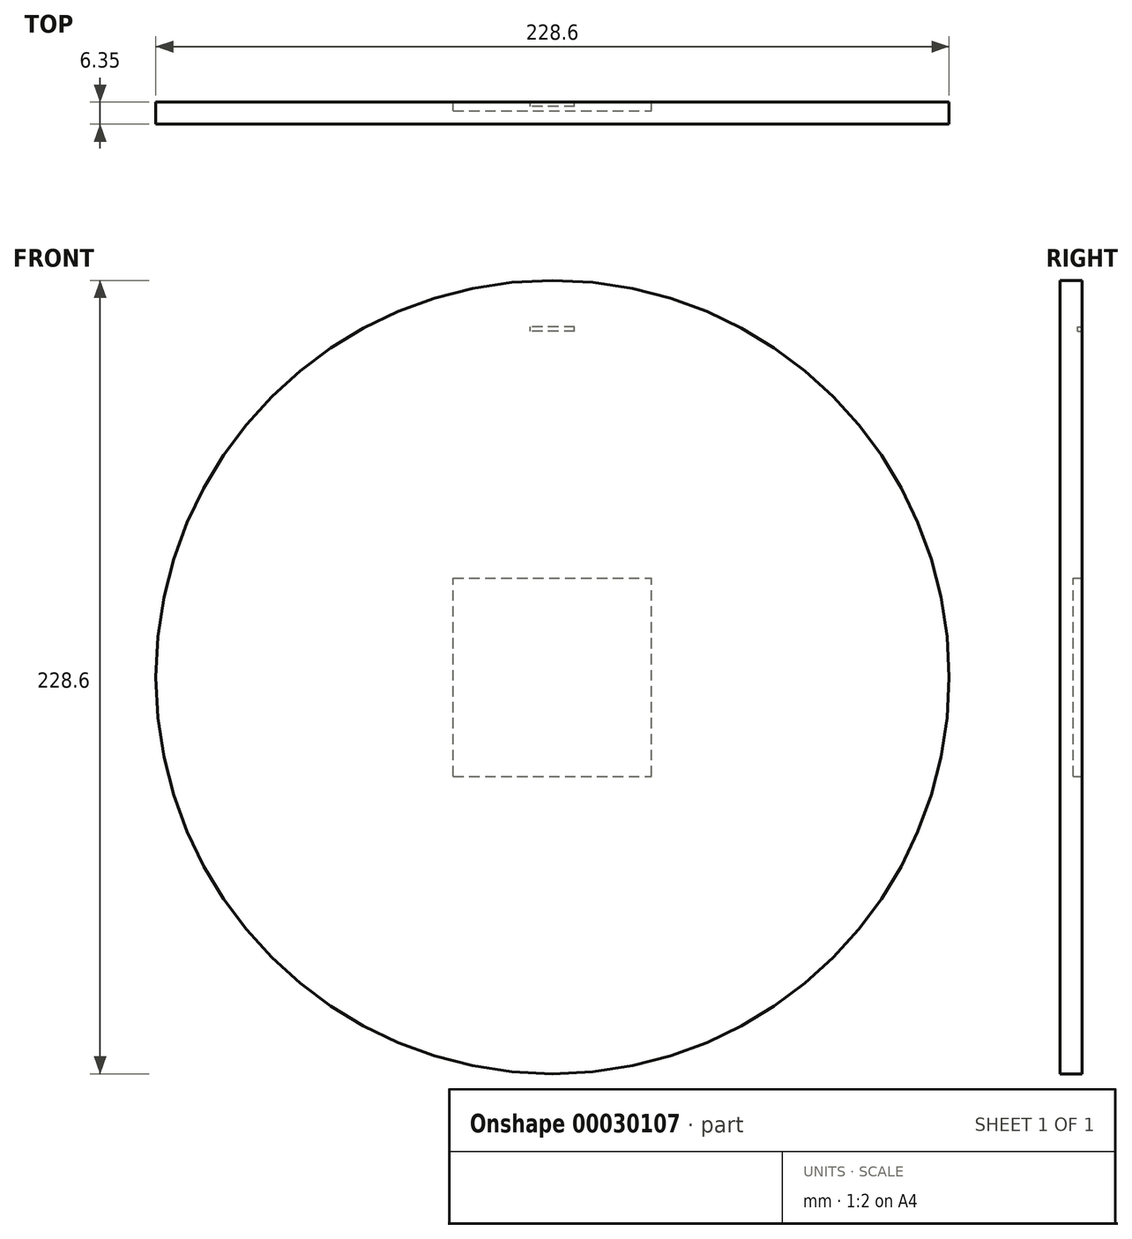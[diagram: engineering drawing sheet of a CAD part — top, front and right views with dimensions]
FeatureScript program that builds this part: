
annotation { "Feature Type Name" : "Feature", "Feature Type Description" : "" }
export const myFeature = defineFeature(function(context is Context, id is Id, definition is map)
    precondition{}
    {
        {
            var Q0;
            Q0=qCreatedBy(makeId("Front.planeOp"),FACE);
            var sketch = newSketch(context, id + "F0", { "sketchPlane" : qUnion([Q0])});
            skCircle(sketch, "E0", {"center": v(0, 0) * mm, "radius": 114.3 * mm});
            skSolve(sketch);
        }
        {
            var Q0;
            Q0 = qSketchRegion(id + "F0", true);
            extrude(context, id + "F1", {"entities" : qUnion([Q0]), "depth" : 25.4 * mm});
        }
        {
            var Q0;
            Q0=makeQuery(id+"F1.opExtrude","CAP_FACE",FACE,{"disambiguationData":[OSD([sQuery(id+"F0.wireOp",EDGE,"E0")])],"isStart":false});
            extrude(context, id + "F2", {"entities" : qUnion([Q0]), "operationType" : NewBodyOperationType.REMOVE, "oppositeDirection" : true, "depth" : 12.7 * mm});
        }
        {
            var Q0;
            Q0=makeQuery(id+"F2.boolean.opBoolean","COPY",FACE,{"derivedFrom":makeQuery(id+"F2.opExtrude","CAP_FACE",FACE,{"disambiguationData":[OSD([sQuery(id+"F0.wireOp",EDGE,"E0")])],"isStart":false})});
            extrude(context, id + "F3", {"entities" : qUnion([Q0]), "operationType" : NewBodyOperationType.REMOVE, "oppositeDirection" : true, "depth" : 6.35 * mm});
        }
        {
            var Q0;
            Q0=makeQuery(id+"F1.opExtrude","CAP_FACE",FACE,{"disambiguationData":[OSD([sQuery(id+"F0.wireOp",EDGE,"E0")])],"isStart":true});
            var sketch = newSketch(context, id + "F4", { "sketchPlane" : qUnion([Q0])});
            skLineSegment(sketch, "E1.rect.bottom", {"start": v(28.58, -28.58) * mm, "end": v(-28.58, -28.58) * mm});
            skLineSegment(sketch, "E1.rect.top", {"start": v(28.58, 28.58) * mm, "end": v(-28.58, 28.58) * mm});
            skLineSegment(sketch, "E1.rect.left", {"start": v(28.57, -28.58) * mm, "end": v(28.58, 28.57) * mm});
            skLineSegment(sketch, "E1.rect.right", {"start": v(-28.58, -28.58) * mm, "end": v(-28.57, 28.57) * mm});
            skPoint(sketch, "E1.rect.middle", {"position": v(0, 0) * mm});
            skSolve(sketch);
        }
        {
            var Q0;
            Q0 = qSketchRegion(id + "F4", true);
            extrude(context, id + "F5", {"entities" : qUnion([Q0]), "operationType" : NewBodyOperationType.REMOVE, "oppositeDirection" : true, "depth" : 2.54 * mm});
        }
        {
            var Q0;
            Q0=makeQuery(id+"F1.opExtrude","CAP_FACE",FACE,{"disambiguationData":[OSD([sQuery(id+"F0.wireOp",EDGE,"E0")])],"isStart":true});
            var sketch = newSketch(context, id + "F6", { "sketchPlane" : qUnion([Q0])});
            skPoint(sketch, "E2", {"position": v(0, 114.3) * mm});
            skPoint(sketch, "E3", {"position": v(0, 99.59) * mm});
            skLineSegment(sketch, "E4.rect.left", {"start": v(6.35, 99.59) * mm, "end": v(6.35, 99.59) * mm});
            skLineSegment(sketch, "E4.rect.right", {"start": v(-6.35, 99.59) * mm, "end": v(-6.35, 99.59) * mm});
            skLineSegment(sketch, "E5.bottom", {"start": v(-6.35, 99.59) * mm, "end": v(6.35, 99.59) * mm});
            skLineSegment(sketch, "E5.top", {"start": v(-6.35, 100.86) * mm, "end": v(6.35, 100.86) * mm});
            skLineSegment(sketch, "E5.left", {"start": v(-6.35, 99.59) * mm, "end": v(-6.35, 100.86) * mm});
            skLineSegment(sketch, "E5.right", {"start": v(6.35, 99.59) * mm, "end": v(6.35, 100.86) * mm});
            skSolve(sketch);
        }
        {
            var Q0;
            Q0=makeQuery(id+"F6.imprint","IMPRINT",FACE,{"disambiguationData":[TD([[makeQuery(id+"F6.imprint","IMPRINT",EDGE,{"derivedFrom":sQuery(id+"F6.wireOp",EDGE,"E5.bottom")}),1.0]])]});
            extrude(context, id + "F7", {"entities" : qUnion([Q0]), "operationType" : NewBodyOperationType.REMOVE, "oppositeDirection" : true, "depth" : 1.27 * mm});
        }
    });
